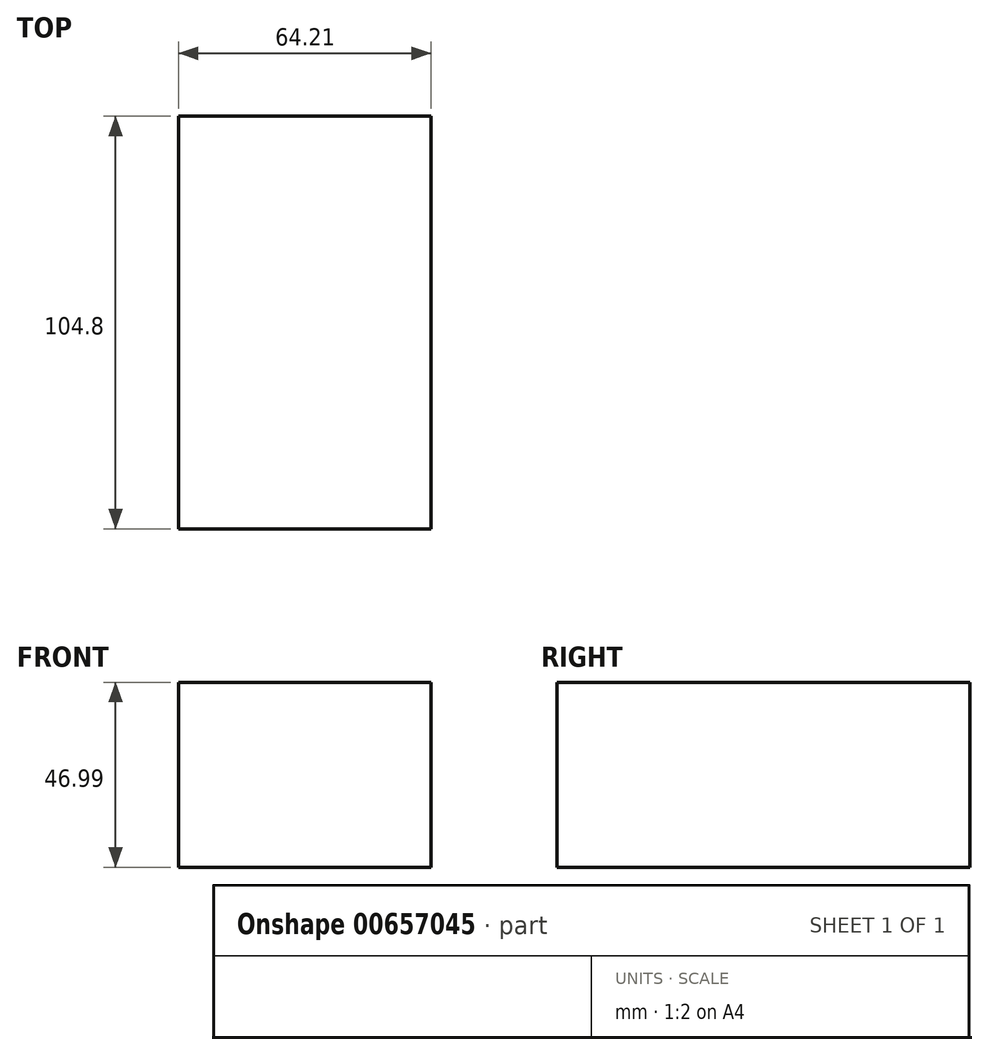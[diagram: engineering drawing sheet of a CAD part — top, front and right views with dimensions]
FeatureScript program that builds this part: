
annotation { "Feature Type Name" : "Feature", "Feature Type Description" : "" }
export const myFeature = defineFeature(function(context is Context, id is Id, definition is map)
    precondition{}
    {
        {
            var Q0;
            Q0=qCreatedBy(makeId("Top.planeOp"),FACE);
            var sketch = newSketch(context, id + "F0", { "sketchPlane" : qUnion([Q0])});
            skLineSegment(sketch, "E0.bottom", {"start": v(-93.56, 63.5) * mm, "end": v(-29.35, 63.5) * mm});
            skLineSegment(sketch, "E0.top", {"start": v(-93.56, -41.31) * mm, "end": v(-29.35, -41.31) * mm});
            skLineSegment(sketch, "E0.left", {"start": v(-93.56, 63.5) * mm, "end": v(-93.56, -41.31) * mm});
            skLineSegment(sketch, "E0.right", {"start": v(-29.35, 63.5) * mm, "end": v(-29.35, -41.31) * mm});
            skSolve(sketch);
        }
        {
            var Q0;
            Q0 = qSketchRegion(id + "F0", true);
            extrude(context, id + "F1", {"entities" : qUnion([Q0]), "depth" : 47 * mm, "offsetDistance" : 25.4 * mm});
        }
    });
